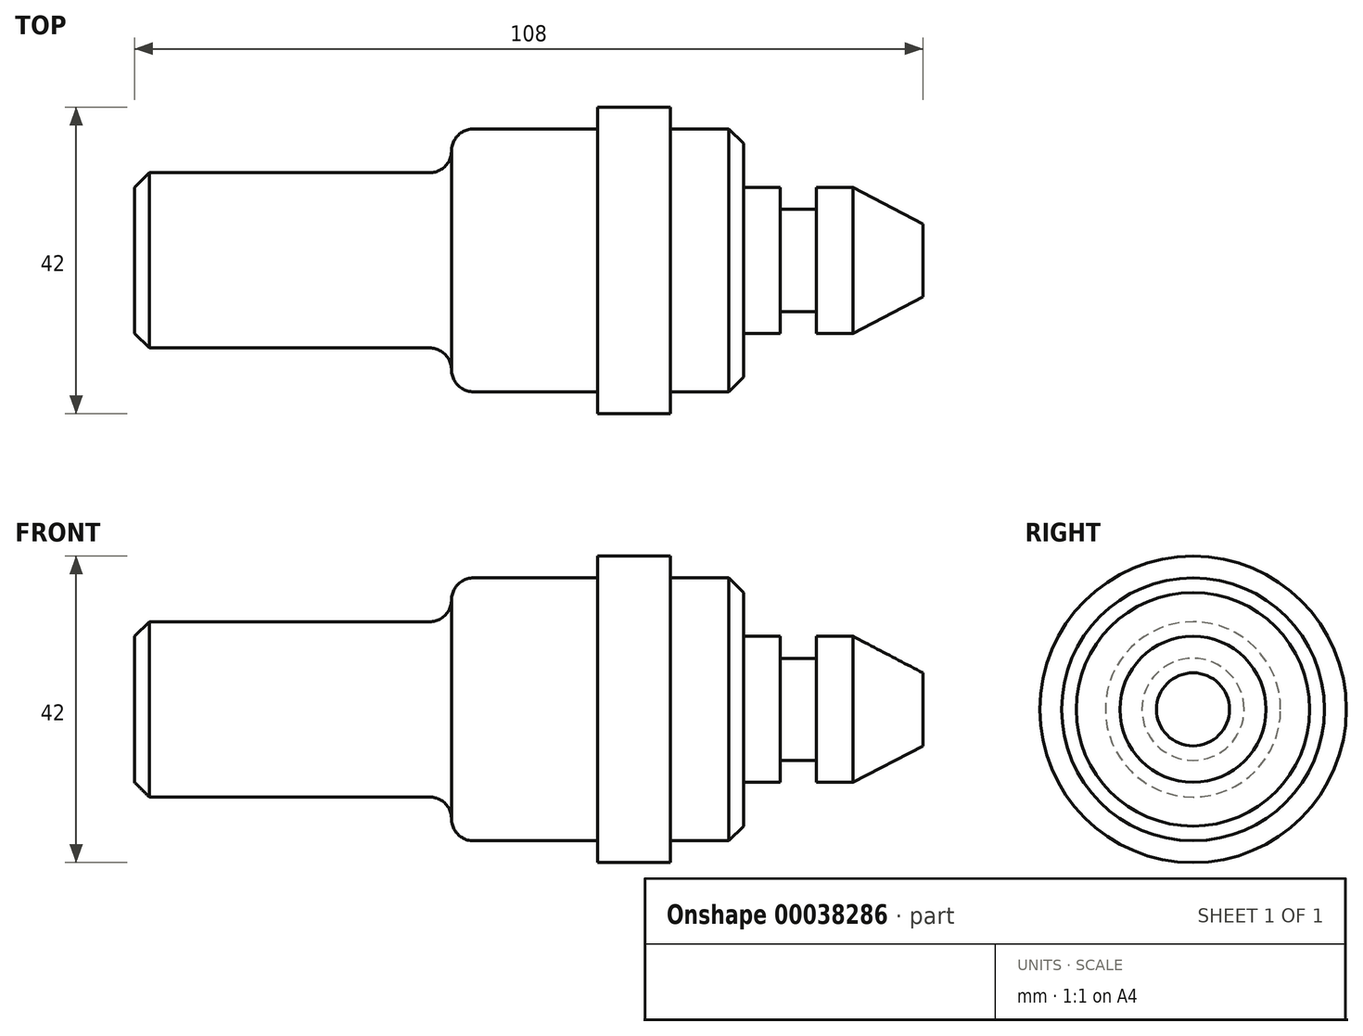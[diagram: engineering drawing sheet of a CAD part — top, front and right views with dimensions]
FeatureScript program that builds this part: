
annotation { "Feature Type Name" : "Feature", "Feature Type Description" : "" }
export const myFeature = defineFeature(function(context is Context, id is Id, definition is map)
    precondition{}
    {
        {
            var Q0;
            Q0=qCreatedBy(makeId("Top.planeOp"),FACE);
            var sketch = newSketch(context, id + "F0", { "sketchPlane" : qUnion([Q0])});
            skLineSegment(sketch, "E0", {"start": v(-62, -10) * mm, "end": v(46, -10) * mm});
            skLineSegment(sketch, "E1", {"start": v(46, -10) * mm, "end": v(46, -5) * mm});
            skLineSegment(sketch, "E2", {"start": v(46, -5) * mm, "end": v(36.42, 0) * mm});
            skLineSegment(sketch, "E3", {"start": v(36.42, 0) * mm, "end": v(31.42, 0) * mm});
            skLineSegment(sketch, "E4", {"start": v(31.42, 0) * mm, "end": v(31.42, -3) * mm});
            skLineSegment(sketch, "E5", {"start": v(31.42, -3) * mm, "end": v(26.42, -3) * mm});
            skLineSegment(sketch, "E6", {"start": v(26.42, -3) * mm, "end": v(26.42, 0) * mm});
            skLineSegment(sketch, "E7", {"start": v(26.42, 0) * mm, "end": v(21.42, 0) * mm});
            skLineSegment(sketch, "E8", {"start": v(21.42, 0) * mm, "end": v(21.42, 8) * mm});
            skLineSegment(sketch, "E9", {"start": v(21.42, 8) * mm, "end": v(11.42, 8) * mm});
            skLineSegment(sketch, "E10", {"start": v(11.42, 8) * mm, "end": v(11.42, 11) * mm});
            skLineSegment(sketch, "E11", {"start": v(11.42, 11) * mm, "end": v(1.42, 11) * mm});
            skLineSegment(sketch, "E12", {"start": v(1.42, 11) * mm, "end": v(1.42, 8) * mm});
            skLineSegment(sketch, "E13", {"start": v(1.42, 8) * mm, "end": v(-18.58, 8) * mm});
            skLineSegment(sketch, "E14", {"start": v(-18.58, 8) * mm, "end": v(-18.58, 2) * mm});
            skLineSegment(sketch, "E15", {"start": v(-18.58, 2) * mm, "end": v(-62, 2) * mm});
            skLineSegment(sketch, "E16", {"start": v(-62, 2) * mm, "end": v(-62, -10) * mm});
            skSolve(sketch);
        }
        {
            var Q0;
            Q0=makeQuery(id+"F0.imprint","IMPRINT",FACE,{"disambiguationData":[TD([[makeQuery(id+"F0.imprint","IMPRINT",EDGE,{"derivedFrom":sQuery(id+"F0.wireOp",EDGE,"E0")}),1.0]])]});
            var Q1;
            Q1=sQuery(id+"F0.wireOp",EDGE,"E0");
            revolve(context, id + "F1", {"entities" : qUnion([Q0]), "axis" : qUnion([Q1]), "revolveType" : RevolveType.FULL});
        }
        {
            var Q0;
            Q0=makeQuery(id+"F1.opRevolve","SWEPT_EDGE",EDGE,{"disambiguationData":[OSD([sQuery(id+"F0.wireOp",EDGE,"E13"),sQuery(id+"F0.wireOp",EDGE,"E14")])]});
            var Q1;
            Q1=makeQuery(id+"F1.opRevolve","SWEPT_EDGE",EDGE,{"disambiguationData":[OSD([sQuery(id+"F0.wireOp",EDGE,"E14"),sQuery(id+"F0.wireOp",EDGE,"E15")])]});
            fillet(context, id + "F2", {"entities" : qUnion([Q0, Q1]), "radius" : 3 * mm, "tangentPropagation" : true, "allowEdgeOverflow" : false});
        }
        {
            var Q0;
            Q0=makeQuery(id+"F1.opRevolve","SWEPT_EDGE",EDGE,{"disambiguationData":[OSD([sQuery(id+"F0.wireOp",EDGE,"E8"),sQuery(id+"F0.wireOp",EDGE,"E9")])]});
            var Q1;
            Q1=makeQuery(id+"F1.opRevolve","SWEPT_EDGE",EDGE,{"disambiguationData":[OSD([sQuery(id+"F0.wireOp",EDGE,"E15"),sQuery(id+"F0.wireOp",EDGE,"E16")])]});
            chamfer(context, id + "F3", {"entities" : qUnion([Q0, Q1]), "width" : 2 * mm, "tangentPropagation" : true});
        }
    });
